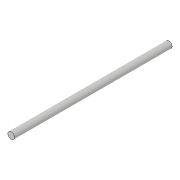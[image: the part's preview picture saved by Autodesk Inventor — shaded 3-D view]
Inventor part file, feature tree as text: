
AUTODESK INVENTOR PART (.ipt)
format: ipt  version: 2018.3 (Build 223284000, 284)  size: 71,168 bytes
history: native  units: in
note: dims shown in document units (in); Inventor stores cm internally (conversion verified against a paired STEP export)
features: extrude x1, sketch x1
ambient origin geometry x8: Origin, YZ Plane, XZ Plane, XY Plane, X Axis, Y Axis, Z Axis, Center Point
bodies: Solid1 (feature_tree)
feature tree (2):
  extrude  "Extrusion1"  Depth=3.0in TaperAngle=0.0deg
  sketch  "Sketch1"  dims[d0=0.125in d1=3.0in d2=0.0in]
